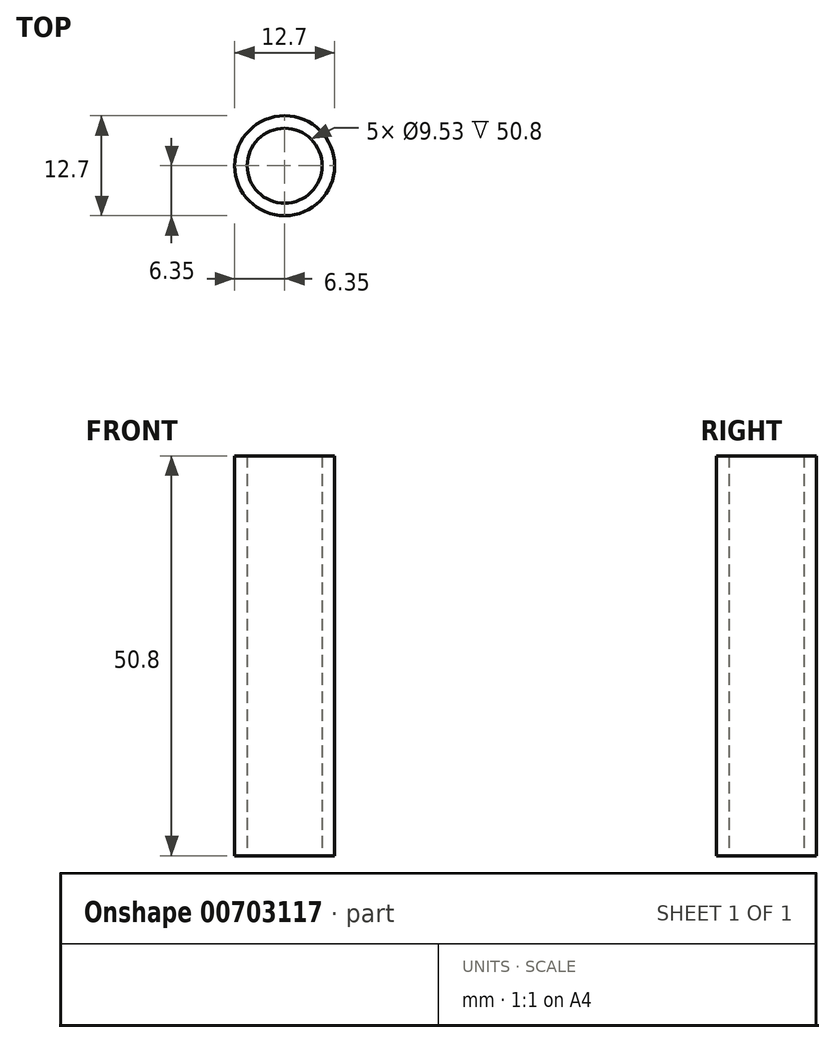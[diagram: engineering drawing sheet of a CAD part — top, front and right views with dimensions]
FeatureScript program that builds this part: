
annotation { "Feature Type Name" : "Feature", "Feature Type Description" : "" }
export const myFeature = defineFeature(function(context is Context, id is Id, definition is map)
    precondition{}
    {
        {
            var Q0;
            Q0=qCreatedBy(makeId("Front.planeOp"),FACE);
            var sketch = newSketch(context, id + "F0", { "sketchPlane" : qUnion([Q0])});
            skLineSegment(sketch, "E0.bottom", {"start": v(6.35, 25.4) * mm, "end": v(4.76, 25.4) * mm});
            skLineSegment(sketch, "E0.top", {"start": v(6.35, -25.4) * mm, "end": v(4.76, -25.4) * mm});
            skLineSegment(sketch, "E0.left", {"start": v(6.35, 25.4) * mm, "end": v(6.35, -25.4) * mm});
            skLineSegment(sketch, "E0.right", {"start": v(4.76, 25.4) * mm, "end": v(4.76, -25.4) * mm});
            skPoint(sketch, "E0.middle", {"position": v(5.56, 0) * mm});
            skLineSegment(sketch, "E1", {"start": v(0, 0) * mm, "end": v(0, 12.97) * mm});
            skSolve(sketch);
        }
        {
            var Q0;
            Q0=makeQuery(id+"F0.imprint","IMPRINT",FACE,{"disambiguationData":[TD([[makeQuery(id+"F0.imprint","IMPRINT",EDGE,{"derivedFrom":sQuery(id+"F0.wireOp",EDGE,"E0.bottom")}),1.0]])]});
            var Q1;
            Q1=sQuery(id+"F0.wireOp",EDGE,"E1");
            revolve(context, id + "F1", {"surfaceOperationType" : NewSurfaceOperationType.NEW, "entities" : qUnion([Q0]), "axis" : qUnion([Q1]), "revolveType" : RevolveType.FULL});
        }
    });
